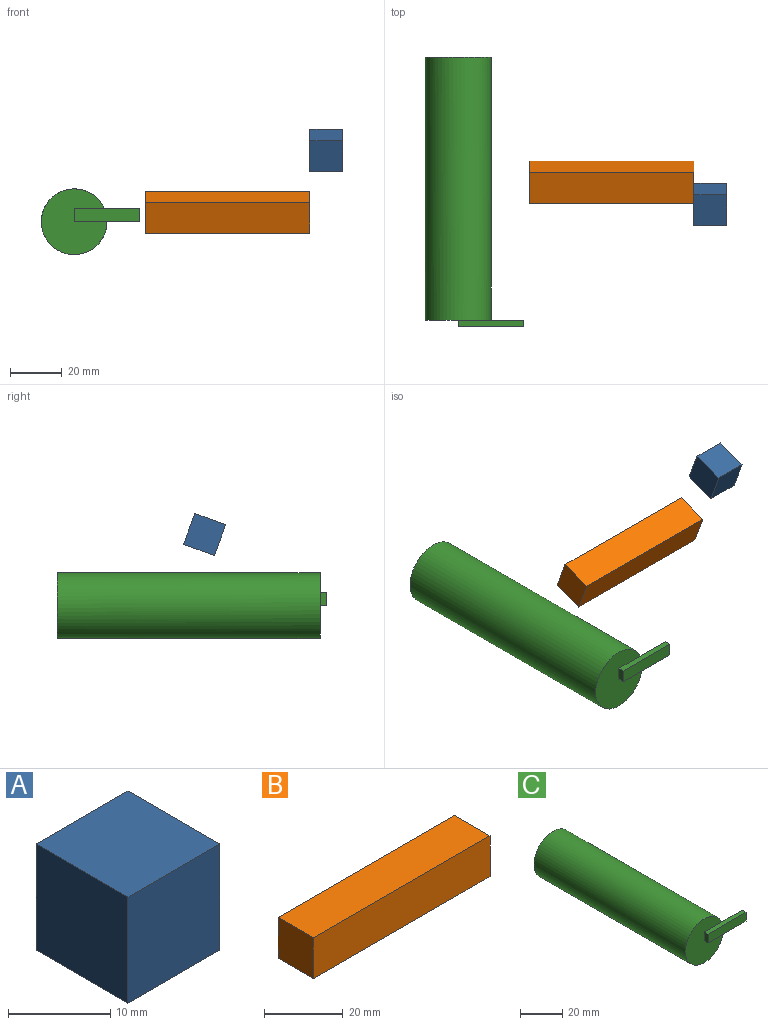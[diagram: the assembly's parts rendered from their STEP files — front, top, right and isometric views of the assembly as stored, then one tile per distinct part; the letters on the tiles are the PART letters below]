
ASSEMBLY  parts=3 mates=1
PART A: 6 faces, bbox 12.7x12.7x12.7 mm
  f0: plane 12.7x12.7mm, normal (0,0,-1), area 161.3mm2, adj f1,f3,f4,f5
  f1: plane 12.7x12.7mm, normal (1,0,0), area 161.3mm2, adj f0,f2,f4,f5
  f2: plane 12.7x12.7mm, normal (0,0,1), area 161.3mm2, adj f1,f3,f4,f5
  f3: plane 12.7x12.7mm, normal (-1,0,0), area 161.3mm2, adj f0,f2,f4,f5
  f4: plane 12.7x12.7mm, normal (0,-1,0), area 161.3mm2, adj f0,f1,f2,f3
  f5: plane 12.7x12.7mm, normal (0,1,0), area 161.3mm2, adj f0,f1,f2,f3
PART B: 6 faces, bbox 63.5x12.7x12.7 mm
  f0: plane 63.5x12.7mm, normal (0,0,-1), area 806.5mm2, adj f1,f3,f4,f5
  f1: plane 12.7x12.7mm, normal (1,0,0), area 161.3mm2, adj f0,f2,f4,f5
  f2: plane 63.5x12.7mm, normal (0,0,1), area 806.5mm2, adj f1,f3,f4,f5
  f3: plane 12.7x12.7mm, normal (-1,0,0), area 161.3mm2, adj f0,f2,f4,f5
  f4: plane 63.5x12.7mm, normal (0,-1,0), area 806.5mm2, adj f0,f1,f2,f3
  f5: plane 63.5x12.7mm, normal (0,1,0), area 806.5mm2, adj f0,f1,f2,f3
PART C: 9 faces, bbox 38.1x104.1x25.4 mm
  f0: plane 25.4x25.4mm, normal (0,-1,0), area 444mm2, adj f1,f4,f5,f6
  f1: cylinder r=12.7mm len=101.6mm, axis (0,1,0), area 8107.3mm2, adj f0,f2,f3
  f2: plane 25.4x25.4mm, normal (0,1,0), area 506.7mm2, adj f1
  f3: plane 13.76x5.08mm, normal (0,1,0), area 66.3mm2, adj f1,f4,f6,f7
  f4: plane 25.4x2.54mm, normal (0,0,1), area 64.5mm2, adj f0,f3,f5,f7,f8
  f5: plane 5.08x2.54mm, normal (-1,0,0), area 12.9mm2, adj f0,f4,f6,f8
  f6: plane 25.4x2.54mm, normal (0,0,-1), area 64.5mm2, adj f0,f3,f5,f7,f8
  f7: plane 5.08x2.54mm, normal (1,0,0), area 12.9mm2, adj f3,f4,f6,f8
  f8: plane 25.4x5.08mm, normal (0,-1,0), area 129mm2, adj f4,f5,f6,f7
PLACE A rot(axis=(1,0,0),20deg) t=(66.53,-17.97,-19.08)mm
PLACE B rot(axis=(1,0,0),20deg) t=(31.74,-33.97,24.88)mm
PLACE C t=(-30.96,23.23,-21.94)mm
MATE slider A.f3 <-> B.f1  axis (-1,0,0) through (60.18,-33.71,5.6)mm
